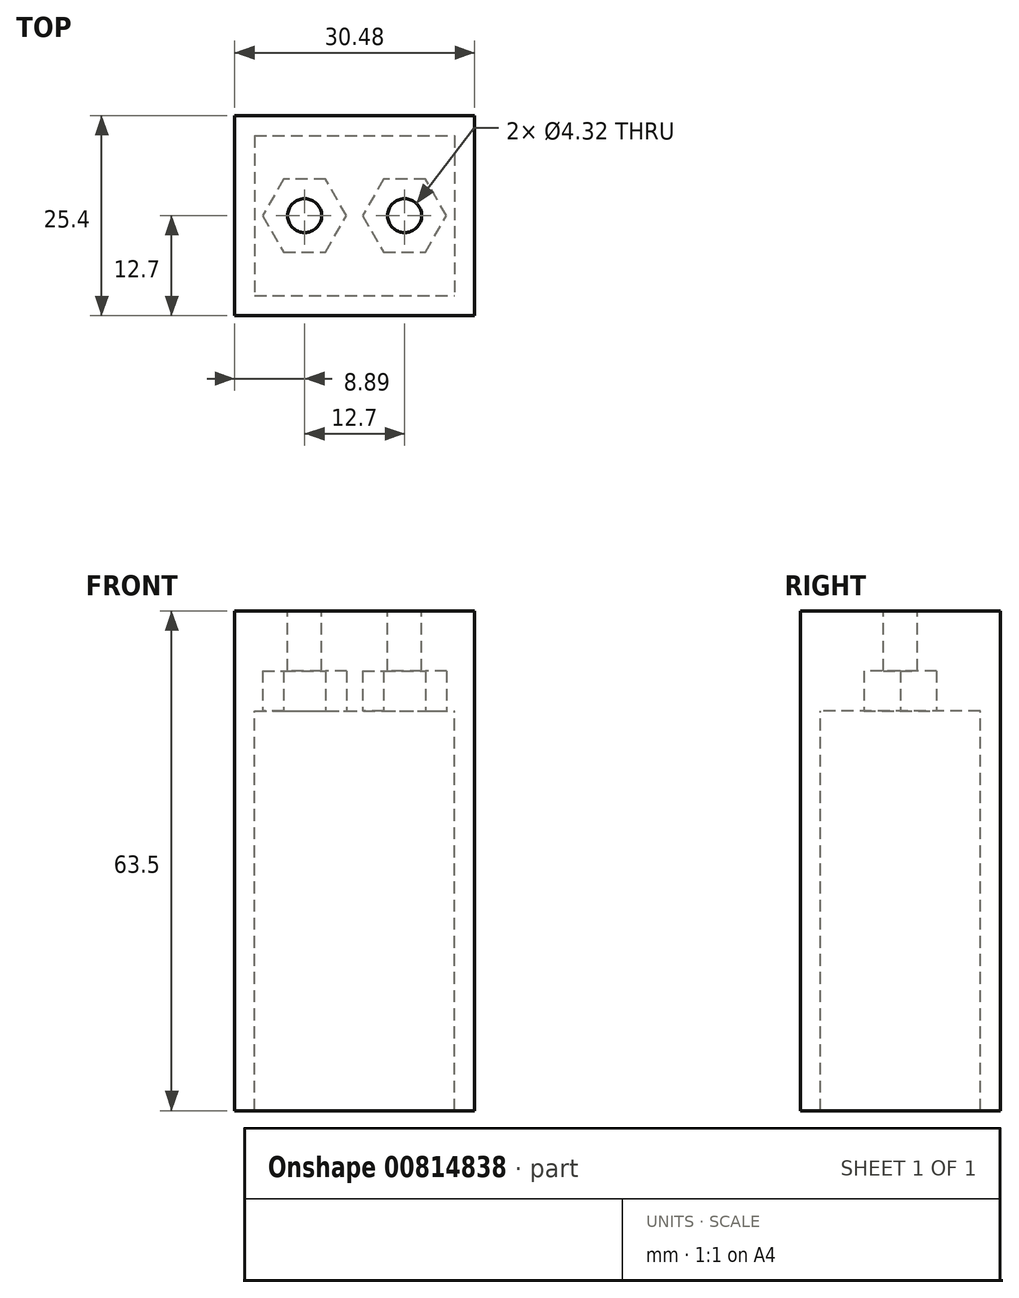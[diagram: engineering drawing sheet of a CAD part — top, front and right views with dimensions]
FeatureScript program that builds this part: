
annotation { "Feature Type Name" : "Feature", "Feature Type Description" : "" }
export const myFeature = defineFeature(function(context is Context, id is Id, definition is map)
    precondition{}
    {
        {
            var Q0;
            Q0=qCreatedBy(makeId("Top.planeOp"),FACE);
            var sketch = newSketch(context, id + "F0", { "sketchPlane" : qUnion([Q0])});
            skLineSegment(sketch, "E0.bottom", {"start": v(-15.24, 12.7) * mm, "end": v(15.24, 12.7) * mm});
            skLineSegment(sketch, "E0.top", {"start": v(-15.24, -12.7) * mm, "end": v(15.24, -12.7) * mm});
            skLineSegment(sketch, "E0.left", {"start": v(-15.24, 12.7) * mm, "end": v(-15.24, -12.7) * mm});
            skLineSegment(sketch, "E0.right", {"start": v(15.24, 12.7) * mm, "end": v(15.24, -12.7) * mm});
            skPoint(sketch, "E0.middle", {"position": v(0, 0) * mm});
            skCircle(sketch, "E1", {"center": v(-6.35, 0) * mm, "radius": 2.16 * mm});
            skCircle(sketch, "E2", {"center": v(6.35, 0) * mm, "radius": 2.16 * mm});
            skLineSegment(sketch, "E3.bottom", {"start": v(-12.7, 10.16) * mm, "end": v(12.7, 10.16) * mm});
            skLineSegment(sketch, "E3.top", {"start": v(-12.7, -10.16) * mm, "end": v(12.7, -10.16) * mm});
            skLineSegment(sketch, "E3.left", {"start": v(-12.7, 10.16) * mm, "end": v(-12.7, -10.16) * mm});
            skLineSegment(sketch, "E3.right", {"start": v(12.7, 10.16) * mm, "end": v(12.7, -10.16) * mm});
            skSolve(sketch);
        }
        {
            var Q0;
            Q0=qSketchRegion(id+"F0",true);
            extrude(context, id + "F1", {"entities" : qUnion([Q0]), "endBound" : BoundingType.SYMMETRIC, "oppositeDirection" : true, "depth" : 63.5 * mm, "offsetDistance" : 25.4 * mm});
        }
        {
            var Q0;
            Q0=makeQuery(id+"F1.opExtrude","CAP_FACE",FACE,{"disambiguationData":[OSD([sQuery(id+"F0.wireOp",EDGE,"E0.bottom"),sQuery(id+"F0.wireOp",EDGE,"E0.top"),sQuery(id+"F0.wireOp",EDGE,"E0.left"),sQuery(id+"F0.wireOp",EDGE,"E0.right"),sQuery(id+"F0.wireOp",EDGE,"E3.bottom"),sQuery(id+"F0.wireOp",EDGE,"E3.top"),sQuery(id+"F0.wireOp",EDGE,"E3.left"),sQuery(id+"F0.wireOp",EDGE,"E3.right")])],"isStart":true});
            var sketch = newSketch(context, id + "F2", { "sketchPlane" : qUnion([Q0])});
            skLineSegment(sketch, "E4.bottom", {"start": v(-12.7, 10.16) * mm, "end": v(12.7, 10.16) * mm});
            skLineSegment(sketch, "E4.top", {"start": v(-12.7, -10.16) * mm, "end": v(12.7, -10.16) * mm});
            skLineSegment(sketch, "E4.left", {"start": v(-12.7, 10.16) * mm, "end": v(-12.7, -10.16) * mm});
            skLineSegment(sketch, "E4.right", {"start": v(12.7, 10.16) * mm, "end": v(12.7, -10.16) * mm});
            skPoint(sketch, "E4.middle", {"position": v(0, 0) * mm});
            skCircle(sketch, "E5", {"center": v(-6.35, 0) * mm, "radius": 2.16 * mm});
            skCircle(sketch, "E6", {"center": v(6.35, 0) * mm, "radius": 2.16 * mm});
            skLineSegment(sketch, "E7.bottom", {"start": v(-10.16, 7.62) * mm, "end": v(10.16, 7.62) * mm});
            skLineSegment(sketch, "E7.top", {"start": v(-10.16, -7.62) * mm, "end": v(10.16, -7.62) * mm});
            skLineSegment(sketch, "E7.left", {"start": v(-10.16, 7.62) * mm, "end": v(-10.16, -7.62) * mm});
            skLineSegment(sketch, "E7.right", {"start": v(10.16, 7.62) * mm, "end": v(10.16, -7.62) * mm});
            skSolve(sketch);
        }
        {
            var Q0;
            Q0=qSketchRegion(id+"F2",true);
            var Q1;
            Q1=makeQuery(id+"F2.imprint","IMPRINT",FACE,{"disambiguationData":[TD([[makeQuery(id+"F2.imprint","IMPRINT",EDGE,{"derivedFrom":sQuery(id+"F2.wireOp",EDGE,"E5")}),-1.0]])]});
            extrude(context, id + "F3", {"entities" : qUnion([Q0, Q1]), "operationType" : NewBodyOperationType.ADD, "oppositeDirection" : true, "depth" : 12.7 * mm, "offsetDistance" : 25.4 * mm});
        }
        {
            var Q0;
            Q0=makeQuery(id+"F3.opExtrude","CAP_FACE",FACE,{"disambiguationData":[OSD([sQuery(id+"F2.wireOp",EDGE,"E4.bottom"),sQuery(id+"F2.wireOp",EDGE,"E4.top"),sQuery(id+"F2.wireOp",EDGE,"E4.left"),sQuery(id+"F2.wireOp",EDGE,"E4.right"),sQuery(id+"F2.wireOp",EDGE,"E5"),sQuery(id+"F2.wireOp",EDGE,"E6")])],"isStart":false});
            var sketch = newSketch(context, id + "F4", { "sketchPlane" : qUnion([Q0])});
            skCircle(sketch, "E8.0", {"center": v(-6.35, 0) * mm, "radius": 2.16 * mm});
            skCircle(sketch, "E9.0", {"center": v(6.35, 0) * mm, "radius": 2.16 * mm});
            skCircle(sketch, "E10", {"center": v(-6.35, 0) * mm, "radius": 5.33 * mm, "construction": true});
            skLineSegment(sketch, "E11.0", {"start": v(-9.02, 4.62) * mm, "end": v(-3.68, 4.62) * mm});
            skLineSegment(sketch, "E11.1", {"start": v(-3.68, 4.62) * mm, "end": v(-1.02, 0) * mm});
            skLineSegment(sketch, "E11.2", {"start": v(-1.02, 0) * mm, "end": v(-3.68, -4.62) * mm});
            skLineSegment(sketch, "E11.3", {"start": v(-3.68, -4.62) * mm, "end": v(-9.02, -4.62) * mm});
            skLineSegment(sketch, "E11.4", {"start": v(-9.02, -4.62) * mm, "end": v(-11.68, 0) * mm});
            skLineSegment(sketch, "E11.5", {"start": v(-11.68, 0) * mm, "end": v(-9.02, 4.62) * mm});
            skCircle(sketch, "E12", {"center": v(6.35, 0) * mm, "radius": 5.33 * mm, "construction": true});
            skLineSegment(sketch, "E13.0", {"start": v(3.68, 4.62) * mm, "end": v(9.02, 4.62) * mm});
            skLineSegment(sketch, "E13.1", {"start": v(9.02, 4.62) * mm, "end": v(11.68, 0) * mm});
            skLineSegment(sketch, "E13.2", {"start": v(11.68, 0) * mm, "end": v(9.02, -4.62) * mm});
            skLineSegment(sketch, "E13.3", {"start": v(9.02, -4.62) * mm, "end": v(3.68, -4.62) * mm});
            skLineSegment(sketch, "E13.4", {"start": v(3.68, -4.62) * mm, "end": v(1.02, 0) * mm});
            skLineSegment(sketch, "E13.5", {"start": v(1.02, 0) * mm, "end": v(3.68, 4.62) * mm});
            skSolve(sketch);
        }
        {
            var Q0;
            Q0=makeQuery(id+"F4.imprint","IMPRINT",FACE,{"disambiguationData":[TD([[makeQuery(id+"F4.imprint","IMPRINT",EDGE,{"derivedFrom":sQuery(id+"F4.wireOp",EDGE,"E9.0")}),1.0]])]});
            var Q1;
            Q1=makeQuery(id+"F4.imprint","IMPRINT",FACE,{"disambiguationData":[TD([[makeQuery(id+"F4.imprint","IMPRINT",EDGE,{"derivedFrom":sQuery(id+"F4.wireOp",EDGE,"E8.0")}),1.0]])]});
            extrude(context, id + "F5", {"entities" : qUnion([Q0, Q1]), "operationType" : NewBodyOperationType.REMOVE, "oppositeDirection" : true, "depth" : 5.08 * mm, "offsetDistance" : 25.4 * mm});
        }
    });
